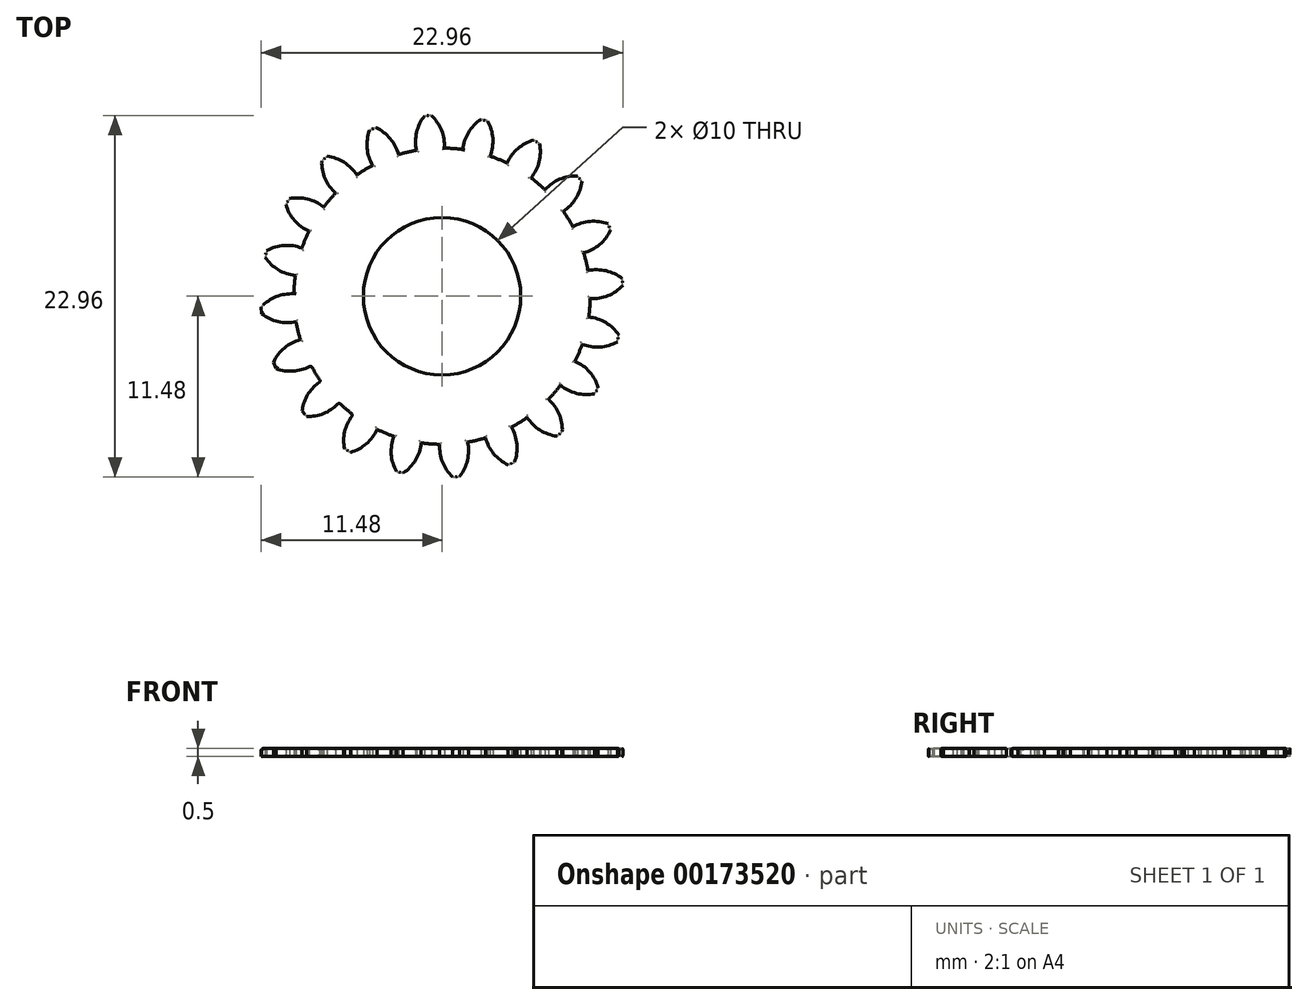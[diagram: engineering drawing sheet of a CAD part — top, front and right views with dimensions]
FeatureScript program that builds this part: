
annotation { "Feature Type Name" : "Feature", "Feature Type Description" : "" }
export const myFeature = defineFeature(function(context is Context, id is Id, definition is map)
    precondition{}
    {
        {
            assignVariable(context, id + "F0", {"name" : "GearDepth", "anyValue" : 0.5});
        }
        {
            assignVariable(context, id + "F1", {"name" : "TeethFillet", "anyValue" : getVariable(context, 'GearDepth') * .25});
        }
        {
            var Q0;
            Q0=qCreatedBy(makeId("Top.planeOp"),FACE);
            var sketch = newSketch(context, id + "F2", { "sketchPlane" : qUnion([Q0])});
            skCircle(sketch, "E0", {"center": v(0, 0) * mm, "radius": 9.4 * mm});
            skCircle(sketch, "E1", {"center": v(0, 0) * mm, "radius": 10.45 * mm, "construction": true});
            skCircle(sketch, "E2", {"center": v(0, 0) * mm, "radius": 11.5 * mm, "construction": true});
            skLineSegment(sketch, "E3", {"start": v(0, 0) * mm, "end": v(0, 17.6) * mm, "construction": true});
            skLineSegment(sketch, "E4", {"start": v(0, 0) * mm, "end": v(-1.42, 18) * mm, "construction": true});
            skLineSegment(sketch, "E5", {"start": v(0, 10.45) * mm, "end": v(-10.54, 10.45) * mm, "construction": true});
            skLineSegment(sketch, "E6", {"start": v(0, 10.45) * mm, "end": v(-10.3, 6.7) * mm, "construction": true});
            skCircle(sketch, "E7", {"center": v(0, 10.45) * mm, "radius": 2.61 * mm, "construction": true});
            skCircle(sketch, "E8", {"center": v(-2.46, 9.56) * mm, "radius": 2.61 * mm, "construction": true});
            skArc(sketch, "E9", {"start": v(-4.91, 10.45) * mm, "mid": v(-4.92, 10.42) * mm, "end": v(-4.94, 10.39) * mm});
            skArc(sketch, "E10.trimOffspring", {"start": v(0.15, 9.4) * mm, "mid": v(-0.03, 10.54) * mm, "end": v(-0.68, 11.48) * mm});
            skArc(sketch, "E11.MirrorCS", {"start": v(-1.62, 9.27) * mm, "mid": v(-1.62, 10.41) * mm, "end": v(-1.12, 11.45) * mm});
            skLineSegment(sketch, "E12", {"start": v(-1.12, 11.45) * mm, "end": v(-0.68, 11.48) * mm});
            skArc(sketch, "E13.1.0", {"start": v(-2.76, 9) * mm, "mid": v(-3.29, 10.01) * mm, "end": v(-4.2, 10.7) * mm});
            skLineSegment(sketch, "E13.1.1", {"start": v(-4.6, 10.54) * mm, "end": v(-4.2, 10.7) * mm});
            skArc(sketch, "E13.1.2", {"start": v(-4.4, 8.31) * mm, "mid": v(-4.76, 9.4) * mm, "end": v(-4.6, 10.54) * mm});
            skArc(sketch, "E13.2.0", {"start": v(-5.4, 7.7) * mm, "mid": v(-6.22, 8.5) * mm, "end": v(-7.3, 8.89) * mm});
            skLineSegment(sketch, "E13.2.1", {"start": v(-7.64, 8.6) * mm, "end": v(-7.3, 8.89) * mm});
            skArc(sketch, "E13.2.2", {"start": v(-6.76, 6.54) * mm, "mid": v(-7.43, 7.47) * mm, "end": v(-7.64, 8.6) * mm});
            skArc(sketch, "E13.3.0", {"start": v(-7.52, 5.65) * mm, "mid": v(-8.54, 6.17) * mm, "end": v(-9.69, 6.2) * mm});
            skLineSegment(sketch, "E13.3.1", {"start": v(-9.92, 5.82) * mm, "end": v(-9.69, 6.2) * mm});
            skArc(sketch, "E13.3.2", {"start": v(-8.45, 4.13) * mm, "mid": v(-9.37, 4.81) * mm, "end": v(-9.92, 5.82) * mm});
            skArc(sketch, "E13.4.0", {"start": v(-8.9, 3.05) * mm, "mid": v(-10.03, 3.23) * mm, "end": v(-11.13, 2.9) * mm});
            skLineSegment(sketch, "E13.4.1", {"start": v(-11.23, 2.47) * mm, "end": v(-11.13, 2.9) * mm});
            skArc(sketch, "E13.4.2", {"start": v(-9.32, 1.32) * mm, "mid": v(-10.4, 1.68) * mm, "end": v(-11.23, 2.47) * mm});
            skArc(sketch, "E13.5.0", {"start": v(-9.4, 0.15) * mm, "mid": v(-10.54, -0.03) * mm, "end": v(-11.48, -0.68) * mm});
            skLineSegment(sketch, "E13.5.1", {"start": v(-11.45, -1.12) * mm, "end": v(-11.48, -0.68) * mm});
            skArc(sketch, "E13.5.2", {"start": v(-9.27, -1.62) * mm, "mid": v(-10.41, -1.62) * mm, "end": v(-11.45, -1.12) * mm});
            skArc(sketch, "E13.6.0", {"start": v(-9, -2.76) * mm, "mid": v(-10.01, -3.29) * mm, "end": v(-10.7, -4.2) * mm});
            skLineSegment(sketch, "E13.6.1", {"start": v(-10.54, -4.6) * mm, "end": v(-10.7, -4.2) * mm});
            skArc(sketch, "E13.6.2", {"start": v(-8.31, -4.4) * mm, "mid": v(-9.4, -4.76) * mm, "end": v(-10.54, -4.6) * mm});
            skArc(sketch, "E13.7.0", {"start": v(-7.7, -5.4) * mm, "mid": v(-8.5, -6.22) * mm, "end": v(-8.89, -7.3) * mm});
            skLineSegment(sketch, "E13.7.1", {"start": v(-8.6, -7.64) * mm, "end": v(-8.89, -7.3) * mm});
            skArc(sketch, "E13.7.2", {"start": v(-6.54, -6.76) * mm, "mid": v(-7.47, -7.43) * mm, "end": v(-8.6, -7.64) * mm});
            skArc(sketch, "E13.8.0", {"start": v(-5.65, -7.52) * mm, "mid": v(-6.17, -8.54) * mm, "end": v(-6.2, -9.69) * mm});
            skLineSegment(sketch, "E13.8.1", {"start": v(-5.82, -9.92) * mm, "end": v(-6.2, -9.69) * mm});
            skArc(sketch, "E13.8.2", {"start": v(-4.13, -8.45) * mm, "mid": v(-4.81, -9.37) * mm, "end": v(-5.82, -9.92) * mm});
            skArc(sketch, "E13.9.0", {"start": v(-3.05, -8.9) * mm, "mid": v(-3.23, -10.03) * mm, "end": v(-2.9, -11.13) * mm});
            skLineSegment(sketch, "E13.9.1", {"start": v(-2.47, -11.23) * mm, "end": v(-2.9, -11.13) * mm});
            skArc(sketch, "E13.9.2", {"start": v(-1.32, -9.32) * mm, "mid": v(-1.68, -10.4) * mm, "end": v(-2.47, -11.23) * mm});
            skArc(sketch, "E13.10.0", {"start": v(-0.15, -9.4) * mm, "mid": v(0.03, -10.54) * mm, "end": v(0.68, -11.48) * mm});
            skLineSegment(sketch, "E13.10.1", {"start": v(1.12, -11.45) * mm, "end": v(0.68, -11.48) * mm});
            skArc(sketch, "E13.10.2", {"start": v(1.62, -9.27) * mm, "mid": v(1.62, -10.41) * mm, "end": v(1.12, -11.45) * mm});
            skArc(sketch, "E13.11.0", {"start": v(2.76, -9) * mm, "mid": v(3.29, -10.01) * mm, "end": v(4.2, -10.7) * mm});
            skLineSegment(sketch, "E13.11.1", {"start": v(4.6, -10.54) * mm, "end": v(4.2, -10.7) * mm});
            skArc(sketch, "E13.11.2", {"start": v(4.4, -8.31) * mm, "mid": v(4.76, -9.4) * mm, "end": v(4.6, -10.54) * mm});
            skArc(sketch, "E13.12.0", {"start": v(5.4, -7.7) * mm, "mid": v(6.22, -8.5) * mm, "end": v(7.3, -8.89) * mm});
            skLineSegment(sketch, "E13.12.1", {"start": v(7.64, -8.6) * mm, "end": v(7.3, -8.89) * mm});
            skArc(sketch, "E13.12.2", {"start": v(6.76, -6.54) * mm, "mid": v(7.43, -7.47) * mm, "end": v(7.64, -8.6) * mm});
            skArc(sketch, "E13.13.0", {"start": v(7.52, -5.65) * mm, "mid": v(8.54, -6.17) * mm, "end": v(9.69, -6.2) * mm});
            skLineSegment(sketch, "E13.13.1", {"start": v(9.92, -5.82) * mm, "end": v(9.69, -6.2) * mm});
            skArc(sketch, "E13.13.2", {"start": v(8.45, -4.13) * mm, "mid": v(9.37, -4.81) * mm, "end": v(9.92, -5.82) * mm});
            skArc(sketch, "E13.14.0", {"start": v(8.9, -3.05) * mm, "mid": v(10.03, -3.23) * mm, "end": v(11.13, -2.9) * mm});
            skLineSegment(sketch, "E13.14.1", {"start": v(11.23, -2.47) * mm, "end": v(11.13, -2.9) * mm});
            skArc(sketch, "E13.14.2", {"start": v(9.32, -1.32) * mm, "mid": v(10.4, -1.68) * mm, "end": v(11.23, -2.47) * mm});
            skArc(sketch, "E13.15.0", {"start": v(9.4, -0.15) * mm, "mid": v(10.54, 0.03) * mm, "end": v(11.48, 0.68) * mm});
            skLineSegment(sketch, "E13.15.1", {"start": v(11.45, 1.12) * mm, "end": v(11.48, 0.68) * mm});
            skArc(sketch, "E13.15.2", {"start": v(9.27, 1.62) * mm, "mid": v(10.41, 1.62) * mm, "end": v(11.45, 1.12) * mm});
            skArc(sketch, "E13.16.0", {"start": v(9, 2.76) * mm, "mid": v(10.01, 3.29) * mm, "end": v(10.7, 4.2) * mm});
            skLineSegment(sketch, "E13.16.1", {"start": v(10.54, 4.6) * mm, "end": v(10.7, 4.2) * mm});
            skArc(sketch, "E13.16.2", {"start": v(8.31, 4.4) * mm, "mid": v(9.4, 4.76) * mm, "end": v(10.54, 4.6) * mm});
            skArc(sketch, "E13.17.0", {"start": v(7.7, 5.4) * mm, "mid": v(8.5, 6.22) * mm, "end": v(8.89, 7.3) * mm});
            skLineSegment(sketch, "E13.17.1", {"start": v(8.6, 7.64) * mm, "end": v(8.89, 7.3) * mm});
            skArc(sketch, "E13.17.2", {"start": v(6.54, 6.76) * mm, "mid": v(7.47, 7.43) * mm, "end": v(8.6, 7.64) * mm});
            skArc(sketch, "E13.18.0", {"start": v(5.65, 7.52) * mm, "mid": v(6.17, 8.54) * mm, "end": v(6.2, 9.69) * mm});
            skLineSegment(sketch, "E13.18.1", {"start": v(5.82, 9.92) * mm, "end": v(6.2, 9.69) * mm});
            skArc(sketch, "E13.18.2", {"start": v(4.13, 8.45) * mm, "mid": v(4.81, 9.37) * mm, "end": v(5.82, 9.92) * mm});
            skArc(sketch, "E13.19.0", {"start": v(3.05, 8.9) * mm, "mid": v(3.23, 10.03) * mm, "end": v(2.9, 11.13) * mm});
            skLineSegment(sketch, "E13.19.1", {"start": v(2.47, 11.23) * mm, "end": v(2.9, 11.13) * mm});
            skArc(sketch, "E13.19.2", {"start": v(1.32, 9.32) * mm, "mid": v(1.68, 10.4) * mm, "end": v(2.47, 11.23) * mm});
            skCircle(sketch, "E14", {"center": v(0, 0) * mm, "radius": 5 * mm});
            skSolve(sketch);
        }
        {
            var Q0;
            {var subQ0=sQuery(id+"F2.wireOp",EDGE,"E10.trimOffspring");Q0=makeQuery(id+"F2.imprint","IMPRINT",FACE,{"disambiguationData":[TD([[makeQuery(id+"F2.imprint","IMPRINT",EDGE,{"derivedFrom":subQ0}),1.0]])]});}
            var Q1;
            {var subQ0=sQuery(id+"F2.wireOp",EDGE,"E0");var subQ1=makeQuery(id+"F2.imprint","INTERSECT",VERTEX,{"derivedFrom":[subQ0,sQuery(id+"F2.wireOp",EDGE,"E10.trimOffspring")]});Q1=makeQuery(id+"F2.imprint","IMPRINT",FACE,{"disambiguationData":[TD([[makeQuery(id+"F2.imprint","IMPRINT",EDGE,{"disambiguationData":[TD([[subQ1,-1.0]])],"derivedFrom":subQ0}),1.0]])]});}
            var Q2;
            {var subQ0=sQuery(id+"F2.wireOp",EDGE,"E13.1.0");Q2=makeQuery(id+"F2.imprint","IMPRINT",FACE,{"disambiguationData":[TD([[makeQuery(id+"F2.imprint","IMPRINT",EDGE,{"derivedFrom":subQ0}),1.0]])]});}
            var Q3;
            {var subQ0=sQuery(id+"F2.wireOp",EDGE,"E13.2.0");Q3=makeQuery(id+"F2.imprint","IMPRINT",FACE,{"disambiguationData":[TD([[makeQuery(id+"F2.imprint","IMPRINT",EDGE,{"derivedFrom":subQ0}),1.0]])]});}
            var Q4;
            {var subQ0=sQuery(id+"F2.wireOp",EDGE,"E13.3.0");Q4=makeQuery(id+"F2.imprint","IMPRINT",FACE,{"disambiguationData":[TD([[makeQuery(id+"F2.imprint","IMPRINT",EDGE,{"derivedFrom":subQ0}),1.0]])]});}
            var Q5;
            {var subQ0=sQuery(id+"F2.wireOp",EDGE,"E13.4.0");Q5=makeQuery(id+"F2.imprint","IMPRINT",FACE,{"disambiguationData":[TD([[makeQuery(id+"F2.imprint","IMPRINT",EDGE,{"derivedFrom":subQ0}),1.0]])]});}
            var Q6;
            {var subQ0=sQuery(id+"F2.wireOp",EDGE,"E13.5.0");Q6=makeQuery(id+"F2.imprint","IMPRINT",FACE,{"disambiguationData":[TD([[makeQuery(id+"F2.imprint","IMPRINT",EDGE,{"derivedFrom":subQ0}),1.0]])]});}
            var Q7;
            {var subQ0=sQuery(id+"F2.wireOp",EDGE,"E13.6.0");Q7=makeQuery(id+"F2.imprint","IMPRINT",FACE,{"disambiguationData":[TD([[makeQuery(id+"F2.imprint","IMPRINT",EDGE,{"derivedFrom":subQ0}),1.0]])]});}
            var Q8;
            {var subQ0=sQuery(id+"F2.wireOp",EDGE,"E13.7.0");Q8=makeQuery(id+"F2.imprint","IMPRINT",FACE,{"disambiguationData":[TD([[makeQuery(id+"F2.imprint","IMPRINT",EDGE,{"derivedFrom":subQ0}),1.0]])]});}
            var Q9;
            {var subQ0=sQuery(id+"F2.wireOp",EDGE,"E13.8.0");Q9=makeQuery(id+"F2.imprint","IMPRINT",FACE,{"disambiguationData":[TD([[makeQuery(id+"F2.imprint","IMPRINT",EDGE,{"derivedFrom":subQ0}),1.0]])]});}
            var Q10;
            {var subQ0=sQuery(id+"F2.wireOp",EDGE,"E13.9.0");Q10=makeQuery(id+"F2.imprint","IMPRINT",FACE,{"disambiguationData":[TD([[makeQuery(id+"F2.imprint","IMPRINT",EDGE,{"derivedFrom":subQ0}),1.0]])]});}
            var Q11;
            {var subQ0=sQuery(id+"F2.wireOp",EDGE,"E13.10.0");Q11=makeQuery(id+"F2.imprint","IMPRINT",FACE,{"disambiguationData":[TD([[makeQuery(id+"F2.imprint","IMPRINT",EDGE,{"derivedFrom":subQ0}),1.0]])]});}
            var Q12;
            {var subQ0=sQuery(id+"F2.wireOp",EDGE,"E13.11.0");Q12=makeQuery(id+"F2.imprint","IMPRINT",FACE,{"disambiguationData":[TD([[makeQuery(id+"F2.imprint","IMPRINT",EDGE,{"derivedFrom":subQ0}),1.0]])]});}
            var Q13;
            {var subQ0=sQuery(id+"F2.wireOp",EDGE,"E13.12.0");Q13=makeQuery(id+"F2.imprint","IMPRINT",FACE,{"disambiguationData":[TD([[makeQuery(id+"F2.imprint","IMPRINT",EDGE,{"derivedFrom":subQ0}),1.0]])]});}
            var Q14;
            {var subQ0=sQuery(id+"F2.wireOp",EDGE,"E13.13.0");Q14=makeQuery(id+"F2.imprint","IMPRINT",FACE,{"disambiguationData":[TD([[makeQuery(id+"F2.imprint","IMPRINT",EDGE,{"derivedFrom":subQ0}),1.0]])]});}
            var Q15;
            {var subQ0=sQuery(id+"F2.wireOp",EDGE,"E13.14.0");Q15=makeQuery(id+"F2.imprint","IMPRINT",FACE,{"disambiguationData":[TD([[makeQuery(id+"F2.imprint","IMPRINT",EDGE,{"derivedFrom":subQ0}),1.0]])]});}
            var Q16;
            {var subQ0=sQuery(id+"F2.wireOp",EDGE,"E13.15.0");Q16=makeQuery(id+"F2.imprint","IMPRINT",FACE,{"disambiguationData":[TD([[makeQuery(id+"F2.imprint","IMPRINT",EDGE,{"derivedFrom":subQ0}),1.0]])]});}
            var Q17;
            {var subQ0=sQuery(id+"F2.wireOp",EDGE,"E13.16.0");Q17=makeQuery(id+"F2.imprint","IMPRINT",FACE,{"disambiguationData":[TD([[makeQuery(id+"F2.imprint","IMPRINT",EDGE,{"derivedFrom":subQ0}),1.0]])]});}
            var Q18;
            {var subQ0=sQuery(id+"F2.wireOp",EDGE,"E13.17.0");Q18=makeQuery(id+"F2.imprint","IMPRINT",FACE,{"disambiguationData":[TD([[makeQuery(id+"F2.imprint","IMPRINT",EDGE,{"derivedFrom":subQ0}),1.0]])]});}
            var Q19;
            {var subQ0=sQuery(id+"F2.wireOp",EDGE,"E13.18.0");Q19=makeQuery(id+"F2.imprint","IMPRINT",FACE,{"disambiguationData":[TD([[makeQuery(id+"F2.imprint","IMPRINT",EDGE,{"derivedFrom":subQ0}),1.0]])]});}
            var Q20;
            {var subQ0=sQuery(id+"F2.wireOp",EDGE,"E13.19.0");Q20=makeQuery(id+"F2.imprint","IMPRINT",FACE,{"disambiguationData":[TD([[makeQuery(id+"F2.imprint","IMPRINT",EDGE,{"derivedFrom":subQ0}),1.0]])]});}
            var Q21;
            Q21=sQuery(id+"F2.wireOp",EDGE,"E0");
            var Q22;
            Q22=sQuery(id+"F2.wireOp",EDGE,"E10.trimOffspring");
            var Q23;
            Q23=sQuery(id+"F2.wireOp",EDGE,"E12");
            var Q24;
            Q24=sQuery(id+"F2.wireOp",EDGE,"E11.MirrorCS");
            extrude(context, id + "F3", {"entities" : qUnion([Q0, Q1, Q2, Q3, Q4, Q5, Q6, Q7, Q8, Q9, Q10, Q11, Q12, Q13, Q14, Q15, Q16, Q17, Q18, Q19, Q20]), "surfaceEntities" : qUnion([Q21, Q22, Q23, Q24]), "depth" : (getVariable(context, 'GearDepth')) * mm});
        }
        {
            var Q0;
            Q0=makeQuery(id+"F3.opExtrude","CAP_EDGE",EDGE,{"disambiguationData":[OSD([sQuery(id+"F2.wireOp",EDGE,"E13.5.2")])],"isStart":false});
            var Q1;
            Q1=makeQuery(id+"F3.opExtrude","CAP_EDGE",EDGE,{"disambiguationData":[OSD([sQuery(id+"F2.wireOp",EDGE,"E13.5.1")])],"isStart":false});
            var Q2;
            {var subQ0=sQuery(id+"F2.wireOp",EDGE,"E0");Q2=makeQuery(id+"F3.opExtrude","CAP_EDGE",EDGE,{"disambiguationData":[OSD([subQ0]),TDD([makeQuery(id+"F2.imprint","IMPRINT",EDGE,{"disambiguationData":[TD([[makeQuery(id+"F2.imprint","INTERSECT",VERTEX,{"derivedFrom":[subQ0,sQuery(id+"F2.wireOp",EDGE,"E13.5.2")]}),-1.0]])],"derivedFrom":subQ0})])],"isStart":false});}
            var Q3;
            Q3=makeQuery(id+"F3.opExtrude","CAP_EDGE",EDGE,{"disambiguationData":[OSD([sQuery(id+"F2.wireOp",EDGE,"E13.6.0")])],"isStart":false});
            var Q4;
            Q4=makeQuery(id+"F3.opExtrude","CAP_EDGE",EDGE,{"disambiguationData":[OSD([sQuery(id+"F2.wireOp",EDGE,"E13.6.1")])],"isStart":false});
            var Q5;
            Q5=makeQuery(id+"F3.opExtrude","CAP_EDGE",EDGE,{"disambiguationData":[OSD([sQuery(id+"F2.wireOp",EDGE,"E13.6.2")])],"isStart":false});
            var Q6;
            {var subQ0=sQuery(id+"F2.wireOp",EDGE,"E0");Q6=makeQuery(id+"F3.opExtrude","SWEPT_FACE",FACE,{"disambiguationData":[OSD([subQ0]),TDD([makeQuery(id+"F2.imprint","IMPRINT",EDGE,{"disambiguationData":[TD([[makeQuery(id+"F2.imprint","INTERSECT",VERTEX,{"derivedFrom":[subQ0,sQuery(id+"F2.wireOp",EDGE,"E13.6.2")]}),-1.0]])],"derivedFrom":subQ0})])]});}
            var Q7;
            {var subQ0=sQuery(id+"F2.wireOp",EDGE,"E0");Q7=makeQuery(id+"F3.opExtrude","CAP_EDGE",EDGE,{"disambiguationData":[OSD([subQ0]),TDD([makeQuery(id+"F2.imprint","IMPRINT",EDGE,{"disambiguationData":[TD([[makeQuery(id+"F2.imprint","INTERSECT",VERTEX,{"derivedFrom":[subQ0,sQuery(id+"F2.wireOp",EDGE,"E13.6.2")]}),-1.0]])],"derivedFrom":subQ0})])],"isStart":false});}
            var Q8;
            Q8=makeQuery(id+"F3.opExtrude","CAP_EDGE",EDGE,{"disambiguationData":[OSD([sQuery(id+"F2.wireOp",EDGE,"E13.7.2")])],"isStart":true});
            var Q9;
            {var subQ0=sQuery(id+"F2.wireOp",EDGE,"E0");Q9=makeQuery(id+"F3.opExtrude","CAP_EDGE",EDGE,{"disambiguationData":[OSD([subQ0]),TDD([makeQuery(id+"F2.imprint","IMPRINT",EDGE,{"disambiguationData":[TD([[makeQuery(id+"F2.imprint","INTERSECT",VERTEX,{"derivedFrom":[subQ0,sQuery(id+"F2.wireOp",EDGE,"E13.7.2")]}),-1.0]])],"derivedFrom":subQ0})])],"isStart":true});}
            var Q10;
            Q10=makeQuery(id+"F3.opExtrude","CAP_EDGE",EDGE,{"disambiguationData":[OSD([sQuery(id+"F2.wireOp",EDGE,"E13.7.2")])],"isStart":false});
            var Q11;
            {var subQ0=sQuery(id+"F2.wireOp",EDGE,"E0");Q11=makeQuery(id+"F3.opExtrude","CAP_EDGE",EDGE,{"disambiguationData":[OSD([subQ0]),TDD([makeQuery(id+"F2.imprint","IMPRINT",EDGE,{"disambiguationData":[TD([[makeQuery(id+"F2.imprint","INTERSECT",VERTEX,{"derivedFrom":[subQ0,sQuery(id+"F2.wireOp",EDGE,"E13.7.2")]}),-1.0]])],"derivedFrom":subQ0})])],"isStart":false});}
            var Q12;
            Q12=makeQuery(id+"F3.opExtrude","CAP_EDGE",EDGE,{"disambiguationData":[OSD([sQuery(id+"F2.wireOp",EDGE,"E13.8.0")])],"isStart":false});
            var Q13;
            {var subQ0=sQuery(id+"F2.wireOp",EDGE,"E0");Q13=makeQuery(id+"F3.opExtrude","SWEPT_FACE",FACE,{"disambiguationData":[OSD([subQ0]),TDD([makeQuery(id+"F2.imprint","IMPRINT",EDGE,{"disambiguationData":[TD([[makeQuery(id+"F2.imprint","INTERSECT",VERTEX,{"derivedFrom":[subQ0,sQuery(id+"F2.wireOp",EDGE,"E13.7.2")]}),-1.0]])],"derivedFrom":subQ0})])]});}
            var Q14;
            Q14=makeQuery(id+"F3.opExtrude","CAP_EDGE",EDGE,{"disambiguationData":[OSD([sQuery(id+"F2.wireOp",EDGE,"E13.6.0")])],"isStart":true});
            var Q15;
            Q15=makeQuery(id+"F3.opExtrude","CAP_EDGE",EDGE,{"disambiguationData":[OSD([sQuery(id+"F2.wireOp",EDGE,"E13.8.2")])],"isStart":false});
            var Q16;
            {var subQ0=sQuery(id+"F2.wireOp",EDGE,"E0");Q16=makeQuery(id+"F3.opExtrude","CAP_EDGE",EDGE,{"disambiguationData":[OSD([subQ0]),TDD([makeQuery(id+"F2.imprint","IMPRINT",EDGE,{"disambiguationData":[TD([[makeQuery(id+"F2.imprint","INTERSECT",VERTEX,{"derivedFrom":[subQ0,sQuery(id+"F2.wireOp",EDGE,"E13.8.2")]}),-1.0]])],"derivedFrom":subQ0})])],"isStart":false});}
            var Q17;
            Q17=makeQuery(id+"F3.opExtrude","CAP_EDGE",EDGE,{"disambiguationData":[OSD([sQuery(id+"F2.wireOp",EDGE,"E13.9.0")])],"isStart":false});
            var Q18;
            Q18=makeQuery(id+"F3.opExtrude","CAP_EDGE",EDGE,{"disambiguationData":[OSD([sQuery(id+"F2.wireOp",EDGE,"E13.9.2")])],"isStart":false});
            var Q19;
            {var subQ0=sQuery(id+"F2.wireOp",EDGE,"E0");Q19=makeQuery(id+"F3.opExtrude","CAP_EDGE",EDGE,{"disambiguationData":[OSD([subQ0]),TDD([makeQuery(id+"F2.imprint","IMPRINT",EDGE,{"disambiguationData":[TD([[makeQuery(id+"F2.imprint","INTERSECT",VERTEX,{"derivedFrom":[subQ0,sQuery(id+"F2.wireOp",EDGE,"E13.9.2")]}),-1.0]])],"derivedFrom":subQ0})])],"isStart":false});}
            var Q20;
            Q20=makeQuery(id+"F3.opExtrude","CAP_EDGE",EDGE,{"disambiguationData":[OSD([sQuery(id+"F2.wireOp",EDGE,"E13.10.0")])],"isStart":false});
            var Q21;
            Q21=makeQuery(id+"F3.opExtrude","CAP_EDGE",EDGE,{"disambiguationData":[OSD([sQuery(id+"F2.wireOp",EDGE,"E13.10.2")])],"isStart":false});
            var Q22;
            {var subQ0=sQuery(id+"F2.wireOp",EDGE,"E0");Q22=makeQuery(id+"F3.opExtrude","CAP_EDGE",EDGE,{"disambiguationData":[OSD([subQ0]),TDD([makeQuery(id+"F2.imprint","IMPRINT",EDGE,{"disambiguationData":[TD([[makeQuery(id+"F2.imprint","INTERSECT",VERTEX,{"derivedFrom":[subQ0,sQuery(id+"F2.wireOp",EDGE,"E13.10.2")]}),-1.0]])],"derivedFrom":subQ0})])],"isStart":false});}
            var Q23;
            Q23=makeQuery(id+"F3.opExtrude","CAP_EDGE",EDGE,{"disambiguationData":[OSD([sQuery(id+"F2.wireOp",EDGE,"E13.11.0")])],"isStart":false});
            var Q24;
            Q24=makeQuery(id+"F3.opExtrude","CAP_EDGE",EDGE,{"disambiguationData":[OSD([sQuery(id+"F2.wireOp",EDGE,"E13.11.2")])],"isStart":false});
            var Q25;
            {var subQ0=sQuery(id+"F2.wireOp",EDGE,"E0");Q25=makeQuery(id+"F3.opExtrude","CAP_EDGE",EDGE,{"disambiguationData":[OSD([subQ0]),TDD([makeQuery(id+"F2.imprint","IMPRINT",EDGE,{"disambiguationData":[TD([[makeQuery(id+"F2.imprint","INTERSECT",VERTEX,{"derivedFrom":[subQ0,sQuery(id+"F2.wireOp",EDGE,"E13.11.2")]}),-1.0]])],"derivedFrom":subQ0})])],"isStart":false});}
            var Q26;
            Q26=makeQuery(id+"F3.opExtrude","CAP_EDGE",EDGE,{"disambiguationData":[OSD([sQuery(id+"F2.wireOp",EDGE,"E13.12.0")])],"isStart":false});
            var Q27;
            Q27=makeQuery(id+"F3.opExtrude","CAP_EDGE",EDGE,{"disambiguationData":[OSD([sQuery(id+"F2.wireOp",EDGE,"E13.12.2")])],"isStart":false});
            var Q28;
            {var subQ0=sQuery(id+"F2.wireOp",EDGE,"E0");Q28=makeQuery(id+"F3.opExtrude","CAP_EDGE",EDGE,{"disambiguationData":[OSD([subQ0]),TDD([makeQuery(id+"F2.imprint","IMPRINT",EDGE,{"disambiguationData":[TD([[makeQuery(id+"F2.imprint","INTERSECT",VERTEX,{"derivedFrom":[subQ0,sQuery(id+"F2.wireOp",EDGE,"E13.12.2")]}),-1.0]])],"derivedFrom":subQ0})])],"isStart":false});}
            var Q29;
            Q29=makeQuery(id+"F3.opExtrude","CAP_EDGE",EDGE,{"disambiguationData":[OSD([sQuery(id+"F2.wireOp",EDGE,"E13.13.0")])],"isStart":false});
            var Q30;
            Q30=makeQuery(id+"F3.opExtrude","CAP_EDGE",EDGE,{"disambiguationData":[OSD([sQuery(id+"F2.wireOp",EDGE,"E13.13.2")])],"isStart":false});
            var Q31;
            {var subQ0=sQuery(id+"F2.wireOp",EDGE,"E0");Q31=makeQuery(id+"F3.opExtrude","CAP_EDGE",EDGE,{"disambiguationData":[OSD([subQ0]),TDD([makeQuery(id+"F2.imprint","IMPRINT",EDGE,{"disambiguationData":[TD([[makeQuery(id+"F2.imprint","INTERSECT",VERTEX,{"derivedFrom":[subQ0,sQuery(id+"F2.wireOp",EDGE,"E13.13.2")]}),-1.0]])],"derivedFrom":subQ0})])],"isStart":false});}
            var Q32;
            Q32=makeQuery(id+"F3.opExtrude","CAP_EDGE",EDGE,{"disambiguationData":[OSD([sQuery(id+"F2.wireOp",EDGE,"E13.14.0")])],"isStart":false});
            var Q33;
            Q33=makeQuery(id+"F3.opExtrude","CAP_EDGE",EDGE,{"disambiguationData":[OSD([sQuery(id+"F2.wireOp",EDGE,"E13.14.2")])],"isStart":false});
            var Q34;
            {var subQ0=sQuery(id+"F2.wireOp",EDGE,"E0");Q34=makeQuery(id+"F3.opExtrude","CAP_EDGE",EDGE,{"disambiguationData":[OSD([subQ0]),TDD([makeQuery(id+"F2.imprint","IMPRINT",EDGE,{"disambiguationData":[TD([[makeQuery(id+"F2.imprint","INTERSECT",VERTEX,{"derivedFrom":[subQ0,sQuery(id+"F2.wireOp",EDGE,"E13.14.2")]}),-1.0]])],"derivedFrom":subQ0})])],"isStart":false});}
            var Q35;
            Q35=makeQuery(id+"F3.opExtrude","CAP_EDGE",EDGE,{"disambiguationData":[OSD([sQuery(id+"F2.wireOp",EDGE,"E13.15.0")])],"isStart":false});
            var Q36;
            {var subQ0=sQuery(id+"F2.wireOp",EDGE,"E0");Q36=makeQuery(id+"F3.opExtrude","CAP_EDGE",EDGE,{"disambiguationData":[OSD([subQ0]),TDD([makeQuery(id+"F2.imprint","IMPRINT",EDGE,{"disambiguationData":[TD([[makeQuery(id+"F2.imprint","INTERSECT",VERTEX,{"derivedFrom":[subQ0,sQuery(id+"F2.wireOp",EDGE,"E13.14.2")]}),-1.0]])],"derivedFrom":subQ0})])],"isStart":false});}
            var Q37;
            Q37=makeQuery(id+"F3.opExtrude","CAP_EDGE",EDGE,{"disambiguationData":[OSD([sQuery(id+"F2.wireOp",EDGE,"E13.15.2")])],"isStart":false});
            var Q38;
            {var subQ0=sQuery(id+"F2.wireOp",EDGE,"E0");Q38=makeQuery(id+"F3.opExtrude","CAP_EDGE",EDGE,{"disambiguationData":[OSD([subQ0]),TDD([makeQuery(id+"F2.imprint","IMPRINT",EDGE,{"disambiguationData":[TD([[makeQuery(id+"F2.imprint","INTERSECT",VERTEX,{"derivedFrom":[subQ0,sQuery(id+"F2.wireOp",EDGE,"E13.15.2")]}),-1.0]])],"derivedFrom":subQ0})])],"isStart":false});}
            var Q39;
            Q39=makeQuery(id+"F3.opExtrude","CAP_EDGE",EDGE,{"disambiguationData":[OSD([sQuery(id+"F2.wireOp",EDGE,"E13.16.0")])],"isStart":false});
            var Q40;
            Q40=makeQuery(id+"F3.opExtrude","CAP_EDGE",EDGE,{"disambiguationData":[OSD([sQuery(id+"F2.wireOp",EDGE,"E13.16.2")])],"isStart":false});
            var Q41;
            Q41=makeQuery(id+"F3.opExtrude","CAP_EDGE",EDGE,{"disambiguationData":[OSD([sQuery(id+"F2.wireOp",EDGE,"E13.17.0")])],"isStart":false});
            var Q42;
            {var subQ0=sQuery(id+"F2.wireOp",EDGE,"E0");Q42=makeQuery(id+"F3.opExtrude","CAP_EDGE",EDGE,{"disambiguationData":[OSD([subQ0]),TDD([makeQuery(id+"F2.imprint","IMPRINT",EDGE,{"disambiguationData":[TD([[makeQuery(id+"F2.imprint","INTERSECT",VERTEX,{"derivedFrom":[subQ0,sQuery(id+"F2.wireOp",EDGE,"E13.16.2")]}),-1.0]])],"derivedFrom":subQ0})])],"isStart":false});}
            var Q43;
            Q43=makeQuery(id+"F3.opExtrude","CAP_EDGE",EDGE,{"disambiguationData":[OSD([sQuery(id+"F2.wireOp",EDGE,"E13.17.2")])],"isStart":false});
            var Q44;
            {var subQ0=sQuery(id+"F2.wireOp",EDGE,"E0");Q44=makeQuery(id+"F3.opExtrude","CAP_EDGE",EDGE,{"disambiguationData":[OSD([subQ0]),TDD([makeQuery(id+"F2.imprint","IMPRINT",EDGE,{"disambiguationData":[TD([[makeQuery(id+"F2.imprint","INTERSECT",VERTEX,{"derivedFrom":[subQ0,sQuery(id+"F2.wireOp",EDGE,"E13.17.2")]}),-1.0]])],"derivedFrom":subQ0})])],"isStart":false});}
            var Q45;
            Q45=makeQuery(id+"F3.opExtrude","CAP_EDGE",EDGE,{"disambiguationData":[OSD([sQuery(id+"F2.wireOp",EDGE,"E13.18.0")])],"isStart":false});
            var Q46;
            Q46=makeQuery(id+"F3.opExtrude","CAP_EDGE",EDGE,{"disambiguationData":[OSD([sQuery(id+"F2.wireOp",EDGE,"E13.18.2")])],"isStart":false});
            var Q47;
            {var subQ0=sQuery(id+"F2.wireOp",EDGE,"E0");Q47=makeQuery(id+"F3.opExtrude","CAP_EDGE",EDGE,{"disambiguationData":[OSD([subQ0]),TDD([makeQuery(id+"F2.imprint","IMPRINT",EDGE,{"disambiguationData":[TD([[makeQuery(id+"F2.imprint","INTERSECT",VERTEX,{"derivedFrom":[subQ0,sQuery(id+"F2.wireOp",EDGE,"E13.18.2")]}),-1.0]])],"derivedFrom":subQ0})])],"isStart":false});}
            var Q48;
            Q48=makeQuery(id+"F3.opExtrude","CAP_EDGE",EDGE,{"disambiguationData":[OSD([sQuery(id+"F2.wireOp",EDGE,"E13.19.0")])],"isStart":false});
            var Q49;
            Q49=makeQuery(id+"F3.opExtrude","CAP_EDGE",EDGE,{"disambiguationData":[OSD([sQuery(id+"F2.wireOp",EDGE,"E13.19.2")])],"isStart":false});
            var Q50;
            Q50=makeQuery(id+"F3.opExtrude","CAP_EDGE",EDGE,{"disambiguationData":[OSD([sQuery(id+"F2.wireOp",EDGE,"E10.trimOffspring")])],"isStart":false});
            var Q51;
            Q51=makeQuery(id+"F3.opExtrude","CAP_EDGE",EDGE,{"disambiguationData":[OSD([sQuery(id+"F2.wireOp",EDGE,"E11.MirrorCS")])],"isStart":false});
            var Q52;
            {var subQ0=sQuery(id+"F2.wireOp",EDGE,"E0");Q52=makeQuery(id+"F3.opExtrude","CAP_EDGE",EDGE,{"disambiguationData":[OSD([subQ0]),TDD([makeQuery(id+"F2.imprint","IMPRINT",EDGE,{"disambiguationData":[TD([[makeQuery(id+"F2.imprint","INTERSECT",VERTEX,{"derivedFrom":[subQ0,sQuery(id+"F2.wireOp",EDGE,"E11.MirrorCS")]}),-1.0]])],"derivedFrom":subQ0})])],"isStart":false});}
            var Q53;
            Q53=makeQuery(id+"F3.opExtrude","CAP_EDGE",EDGE,{"disambiguationData":[OSD([sQuery(id+"F2.wireOp",EDGE,"E13.1.0")])],"isStart":false});
            var Q54;
            Q54=makeQuery(id+"F3.opExtrude","CAP_EDGE",EDGE,{"disambiguationData":[OSD([sQuery(id+"F2.wireOp",EDGE,"E13.1.2")])],"isStart":false});
            var Q55;
            {var subQ0=sQuery(id+"F2.wireOp",EDGE,"E0");Q55=makeQuery(id+"F3.opExtrude","CAP_EDGE",EDGE,{"disambiguationData":[OSD([subQ0]),TDD([makeQuery(id+"F2.imprint","IMPRINT",EDGE,{"disambiguationData":[TD([[makeQuery(id+"F2.imprint","INTERSECT",VERTEX,{"derivedFrom":[subQ0,sQuery(id+"F2.wireOp",EDGE,"E13.1.2")]}),-1.0]])],"derivedFrom":subQ0})])],"isStart":false});}
            var Q56;
            Q56=makeQuery(id+"F3.opExtrude","CAP_EDGE",EDGE,{"disambiguationData":[OSD([sQuery(id+"F2.wireOp",EDGE,"E13.2.0")])],"isStart":false});
            var Q57;
            Q57=makeQuery(id+"F3.opExtrude","CAP_EDGE",EDGE,{"disambiguationData":[OSD([sQuery(id+"F2.wireOp",EDGE,"E13.2.2")])],"isStart":false});
            var Q58;
            {var subQ0=sQuery(id+"F2.wireOp",EDGE,"E0");Q58=makeQuery(id+"F3.opExtrude","CAP_EDGE",EDGE,{"disambiguationData":[OSD([subQ0]),TDD([makeQuery(id+"F2.imprint","IMPRINT",EDGE,{"disambiguationData":[TD([[makeQuery(id+"F2.imprint","INTERSECT",VERTEX,{"derivedFrom":[subQ0,sQuery(id+"F2.wireOp",EDGE,"E13.2.2")]}),-1.0]])],"derivedFrom":subQ0})])],"isStart":false});}
            var Q59;
            Q59=makeQuery(id+"F3.opExtrude","CAP_EDGE",EDGE,{"disambiguationData":[OSD([sQuery(id+"F2.wireOp",EDGE,"E13.3.0")])],"isStart":false});
            var Q60;
            Q60=makeQuery(id+"F3.opExtrude","CAP_EDGE",EDGE,{"disambiguationData":[OSD([sQuery(id+"F2.wireOp",EDGE,"E13.3.2")])],"isStart":false});
            var Q61;
            {var subQ0=sQuery(id+"F2.wireOp",EDGE,"E0");Q61=makeQuery(id+"F3.opExtrude","CAP_EDGE",EDGE,{"disambiguationData":[OSD([subQ0]),TDD([makeQuery(id+"F2.imprint","IMPRINT",EDGE,{"disambiguationData":[TD([[makeQuery(id+"F2.imprint","INTERSECT",VERTEX,{"derivedFrom":[subQ0,sQuery(id+"F2.wireOp",EDGE,"E13.3.2")]}),-1.0]])],"derivedFrom":subQ0})])],"isStart":false});}
            var Q62;
            Q62=makeQuery(id+"F3.opExtrude","CAP_EDGE",EDGE,{"disambiguationData":[OSD([sQuery(id+"F2.wireOp",EDGE,"E13.4.0")])],"isStart":false});
            var Q63;
            Q63=makeQuery(id+"F3.opExtrude","CAP_EDGE",EDGE,{"disambiguationData":[OSD([sQuery(id+"F2.wireOp",EDGE,"E13.4.2")])],"isStart":false});
            var Q64;
            {var subQ0=sQuery(id+"F2.wireOp",EDGE,"E0");Q64=makeQuery(id+"F3.opExtrude","CAP_EDGE",EDGE,{"disambiguationData":[OSD([subQ0]),TDD([makeQuery(id+"F2.imprint","IMPRINT",EDGE,{"disambiguationData":[TD([[makeQuery(id+"F2.imprint","INTERSECT",VERTEX,{"derivedFrom":[subQ0,sQuery(id+"F2.wireOp",EDGE,"E13.4.2")]}),-1.0]])],"derivedFrom":subQ0})])],"isStart":false});}
            var Q65;
            {var subQ0=sQuery(id+"F2.wireOp",EDGE,"E0");Q65=makeQuery(id+"F3.opExtrude","CAP_EDGE",EDGE,{"disambiguationData":[OSD([subQ0]),TDD([makeQuery(id+"F2.imprint","IMPRINT",EDGE,{"disambiguationData":[TD([[makeQuery(id+"F2.imprint","INTERSECT",VERTEX,{"derivedFrom":[subQ0,sQuery(id+"F2.wireOp",EDGE,"E13.5.2")]}),-1.0]])],"derivedFrom":subQ0})])],"isStart":true});}
            var Q66;
            Q66=makeQuery(id+"F3.opExtrude","CAP_EDGE",EDGE,{"disambiguationData":[OSD([sQuery(id+"F2.wireOp",EDGE,"E13.5.2")])],"isStart":true});
            var Q67;
            {var subQ0=sQuery(id+"F2.wireOp",EDGE,"E0");Q67=makeQuery(id+"F3.opExtrude","CAP_EDGE",EDGE,{"disambiguationData":[OSD([subQ0]),TDD([makeQuery(id+"F2.imprint","IMPRINT",EDGE,{"disambiguationData":[TD([[makeQuery(id+"F2.imprint","INTERSECT",VERTEX,{"derivedFrom":[subQ0,sQuery(id+"F2.wireOp",EDGE,"E13.4.2")]}),-1.0]])],"derivedFrom":subQ0})])],"isStart":true});}
            var Q68;
            Q68=makeQuery(id+"F3.opExtrude","CAP_EDGE",EDGE,{"disambiguationData":[OSD([sQuery(id+"F2.wireOp",EDGE,"E13.4.2")])],"isStart":true});
            var Q69;
            Q69=makeQuery(id+"F3.opExtrude","CAP_EDGE",EDGE,{"disambiguationData":[OSD([sQuery(id+"F2.wireOp",EDGE,"E13.4.0")])],"isStart":true});
            var Q70;
            {var subQ0=sQuery(id+"F2.wireOp",EDGE,"E0");Q70=makeQuery(id+"F3.opExtrude","CAP_EDGE",EDGE,{"disambiguationData":[OSD([subQ0]),TDD([makeQuery(id+"F2.imprint","IMPRINT",EDGE,{"disambiguationData":[TD([[makeQuery(id+"F2.imprint","INTERSECT",VERTEX,{"derivedFrom":[subQ0,sQuery(id+"F2.wireOp",EDGE,"E13.3.2")]}),-1.0]])],"derivedFrom":subQ0})])],"isStart":true});}
            var Q71;
            Q71=makeQuery(id+"F3.opExtrude","CAP_EDGE",EDGE,{"disambiguationData":[OSD([sQuery(id+"F2.wireOp",EDGE,"E13.3.2")])],"isStart":true});
            var Q72;
            Q72=makeQuery(id+"F3.opExtrude","CAP_EDGE",EDGE,{"disambiguationData":[OSD([sQuery(id+"F2.wireOp",EDGE,"E13.3.0")])],"isStart":true});
            var Q73;
            {var subQ0=sQuery(id+"F2.wireOp",EDGE,"E0");Q73=makeQuery(id+"F3.opExtrude","CAP_EDGE",EDGE,{"disambiguationData":[OSD([subQ0]),TDD([makeQuery(id+"F2.imprint","IMPRINT",EDGE,{"disambiguationData":[TD([[makeQuery(id+"F2.imprint","INTERSECT",VERTEX,{"derivedFrom":[subQ0,sQuery(id+"F2.wireOp",EDGE,"E13.2.2")]}),-1.0]])],"derivedFrom":subQ0})])],"isStart":true});}
            var Q74;
            Q74=makeQuery(id+"F3.opExtrude","CAP_EDGE",EDGE,{"disambiguationData":[OSD([sQuery(id+"F2.wireOp",EDGE,"E13.2.2")])],"isStart":true});
            var Q75;
            Q75=makeQuery(id+"F3.opExtrude","CAP_EDGE",EDGE,{"disambiguationData":[OSD([sQuery(id+"F2.wireOp",EDGE,"E13.2.0")])],"isStart":true});
            var Q76;
            Q76=makeQuery(id+"F3.opExtrude","CAP_EDGE",EDGE,{"disambiguationData":[OSD([sQuery(id+"F2.wireOp",EDGE,"E13.1.2")])],"isStart":true});
            var Q77;
            {var subQ0=sQuery(id+"F2.wireOp",EDGE,"E0");Q77=makeQuery(id+"F3.opExtrude","CAP_EDGE",EDGE,{"disambiguationData":[OSD([subQ0]),TDD([makeQuery(id+"F2.imprint","IMPRINT",EDGE,{"disambiguationData":[TD([[makeQuery(id+"F2.imprint","INTERSECT",VERTEX,{"derivedFrom":[subQ0,sQuery(id+"F2.wireOp",EDGE,"E13.1.2")]}),-1.0]])],"derivedFrom":subQ0})])],"isStart":true});}
            var Q78;
            Q78=makeQuery(id+"F3.opExtrude","CAP_EDGE",EDGE,{"disambiguationData":[OSD([sQuery(id+"F2.wireOp",EDGE,"E13.1.0")])],"isStart":true});
            var Q79;
            {var subQ0=sQuery(id+"F2.wireOp",EDGE,"E0");Q79=makeQuery(id+"F3.opExtrude","CAP_EDGE",EDGE,{"disambiguationData":[OSD([subQ0]),TDD([makeQuery(id+"F2.imprint","IMPRINT",EDGE,{"disambiguationData":[TD([[makeQuery(id+"F2.imprint","INTERSECT",VERTEX,{"derivedFrom":[subQ0,sQuery(id+"F2.wireOp",EDGE,"E11.MirrorCS")]}),-1.0]])],"derivedFrom":subQ0})])],"isStart":true});}
            var Q80;
            Q80=makeQuery(id+"F3.opExtrude","CAP_EDGE",EDGE,{"disambiguationData":[OSD([sQuery(id+"F2.wireOp",EDGE,"E11.MirrorCS")])],"isStart":true});
            var Q81;
            Q81=makeQuery(id+"F3.opExtrude","CAP_EDGE",EDGE,{"disambiguationData":[OSD([sQuery(id+"F2.wireOp",EDGE,"E10.trimOffspring")])],"isStart":true});
            var Q82;
            {var subQ0=sQuery(id+"F2.wireOp",EDGE,"E0");Q82=makeQuery(id+"F3.opExtrude","CAP_EDGE",EDGE,{"disambiguationData":[OSD([subQ0]),TDD([makeQuery(id+"F2.imprint","IMPRINT",EDGE,{"disambiguationData":[TD([[makeQuery(id+"F2.imprint","INTERSECT",VERTEX,{"derivedFrom":[subQ0,sQuery(id+"F2.wireOp",EDGE,"E10.trimOffspring")]}),1.0]])],"derivedFrom":subQ0})])],"isStart":true});}
            var Q83;
            Q83=makeQuery(id+"F3.opExtrude","CAP_EDGE",EDGE,{"disambiguationData":[OSD([sQuery(id+"F2.wireOp",EDGE,"E13.19.2")])],"isStart":true});
            var Q84;
            Q84=makeQuery(id+"F3.opExtrude","CAP_EDGE",EDGE,{"disambiguationData":[OSD([sQuery(id+"F2.wireOp",EDGE,"E13.19.0")])],"isStart":true});
            var Q85;
            {var subQ0=sQuery(id+"F2.wireOp",EDGE,"E0");Q85=makeQuery(id+"F3.opExtrude","CAP_EDGE",EDGE,{"disambiguationData":[OSD([subQ0]),TDD([makeQuery(id+"F2.imprint","IMPRINT",EDGE,{"disambiguationData":[TD([[makeQuery(id+"F2.imprint","INTERSECT",VERTEX,{"derivedFrom":[subQ0,sQuery(id+"F2.wireOp",EDGE,"E13.18.2")]}),-1.0]])],"derivedFrom":subQ0})])],"isStart":true});}
            var Q86;
            Q86=makeQuery(id+"F3.opExtrude","CAP_EDGE",EDGE,{"disambiguationData":[OSD([sQuery(id+"F2.wireOp",EDGE,"E13.18.2")])],"isStart":true});
            var Q87;
            Q87=makeQuery(id+"F3.opExtrude","CAP_EDGE",EDGE,{"disambiguationData":[OSD([sQuery(id+"F2.wireOp",EDGE,"E13.18.0")])],"isStart":true});
            var Q88;
            {var subQ0=sQuery(id+"F2.wireOp",EDGE,"E0");Q88=makeQuery(id+"F3.opExtrude","CAP_EDGE",EDGE,{"disambiguationData":[OSD([subQ0]),TDD([makeQuery(id+"F2.imprint","IMPRINT",EDGE,{"disambiguationData":[TD([[makeQuery(id+"F2.imprint","INTERSECT",VERTEX,{"derivedFrom":[subQ0,sQuery(id+"F2.wireOp",EDGE,"E13.17.2")]}),-1.0]])],"derivedFrom":subQ0})])],"isStart":true});}
            var Q89;
            Q89=makeQuery(id+"F3.opExtrude","CAP_EDGE",EDGE,{"disambiguationData":[OSD([sQuery(id+"F2.wireOp",EDGE,"E13.17.2")])],"isStart":true});
            var Q90;
            Q90=makeQuery(id+"F3.opExtrude","CAP_EDGE",EDGE,{"disambiguationData":[OSD([sQuery(id+"F2.wireOp",EDGE,"E13.17.0")])],"isStart":true});
            var Q91;
            {var subQ0=sQuery(id+"F2.wireOp",EDGE,"E0");Q91=makeQuery(id+"F3.opExtrude","CAP_EDGE",EDGE,{"disambiguationData":[OSD([subQ0]),TDD([makeQuery(id+"F2.imprint","IMPRINT",EDGE,{"disambiguationData":[TD([[makeQuery(id+"F2.imprint","INTERSECT",VERTEX,{"derivedFrom":[subQ0,sQuery(id+"F2.wireOp",EDGE,"E13.16.2")]}),-1.0]])],"derivedFrom":subQ0})])],"isStart":true});}
            var Q92;
            Q92=makeQuery(id+"F3.opExtrude","CAP_EDGE",EDGE,{"disambiguationData":[OSD([sQuery(id+"F2.wireOp",EDGE,"E13.16.2")])],"isStart":true});
            var Q93;
            Q93=makeQuery(id+"F3.opExtrude","CAP_EDGE",EDGE,{"disambiguationData":[OSD([sQuery(id+"F2.wireOp",EDGE,"E13.16.0")])],"isStart":true});
            var Q94;
            {var subQ0=sQuery(id+"F2.wireOp",EDGE,"E0");Q94=makeQuery(id+"F3.opExtrude","CAP_EDGE",EDGE,{"disambiguationData":[OSD([subQ0]),TDD([makeQuery(id+"F2.imprint","IMPRINT",EDGE,{"disambiguationData":[TD([[makeQuery(id+"F2.imprint","INTERSECT",VERTEX,{"derivedFrom":[subQ0,sQuery(id+"F2.wireOp",EDGE,"E13.15.2")]}),-1.0]])],"derivedFrom":subQ0})])],"isStart":true});}
            var Q95;
            Q95=makeQuery(id+"F3.opExtrude","CAP_EDGE",EDGE,{"disambiguationData":[OSD([sQuery(id+"F2.wireOp",EDGE,"E13.15.2")])],"isStart":true});
            var Q96;
            Q96=makeQuery(id+"F3.opExtrude","CAP_EDGE",EDGE,{"disambiguationData":[OSD([sQuery(id+"F2.wireOp",EDGE,"E13.15.0")])],"isStart":true});
            var Q97;
            {var subQ0=sQuery(id+"F2.wireOp",EDGE,"E0");Q97=makeQuery(id+"F3.opExtrude","CAP_EDGE",EDGE,{"disambiguationData":[OSD([subQ0]),TDD([makeQuery(id+"F2.imprint","IMPRINT",EDGE,{"disambiguationData":[TD([[makeQuery(id+"F2.imprint","INTERSECT",VERTEX,{"derivedFrom":[subQ0,sQuery(id+"F2.wireOp",EDGE,"E13.14.2")]}),-1.0]])],"derivedFrom":subQ0})])],"isStart":true});}
            var Q98;
            Q98=makeQuery(id+"F3.opExtrude","CAP_EDGE",EDGE,{"disambiguationData":[OSD([sQuery(id+"F2.wireOp",EDGE,"E13.14.2")])],"isStart":true});
            var Q99;
            Q99=makeQuery(id+"F3.opExtrude","CAP_EDGE",EDGE,{"disambiguationData":[OSD([sQuery(id+"F2.wireOp",EDGE,"E13.14.0")])],"isStart":true});
            var Q100;
            {var subQ0=sQuery(id+"F2.wireOp",EDGE,"E0");Q100=makeQuery(id+"F3.opExtrude","CAP_EDGE",EDGE,{"disambiguationData":[OSD([subQ0]),TDD([makeQuery(id+"F2.imprint","IMPRINT",EDGE,{"disambiguationData":[TD([[makeQuery(id+"F2.imprint","INTERSECT",VERTEX,{"derivedFrom":[subQ0,sQuery(id+"F2.wireOp",EDGE,"E13.13.2")]}),-1.0]])],"derivedFrom":subQ0})])],"isStart":true});}
            var Q101;
            Q101=makeQuery(id+"F3.opExtrude","CAP_EDGE",EDGE,{"disambiguationData":[OSD([sQuery(id+"F2.wireOp",EDGE,"E13.13.2")])],"isStart":true});
            var Q102;
            Q102=makeQuery(id+"F3.opExtrude","CAP_EDGE",EDGE,{"disambiguationData":[OSD([sQuery(id+"F2.wireOp",EDGE,"E13.13.0")])],"isStart":true});
            var Q103;
            {var subQ0=sQuery(id+"F2.wireOp",EDGE,"E0");Q103=makeQuery(id+"F3.opExtrude","CAP_EDGE",EDGE,{"disambiguationData":[OSD([subQ0]),TDD([makeQuery(id+"F2.imprint","IMPRINT",EDGE,{"disambiguationData":[TD([[makeQuery(id+"F2.imprint","INTERSECT",VERTEX,{"derivedFrom":[subQ0,sQuery(id+"F2.wireOp",EDGE,"E13.12.2")]}),-1.0]])],"derivedFrom":subQ0})])],"isStart":true});}
            var Q104;
            Q104=makeQuery(id+"F3.opExtrude","CAP_EDGE",EDGE,{"disambiguationData":[OSD([sQuery(id+"F2.wireOp",EDGE,"E13.12.2")])],"isStart":true});
            var Q105;
            Q105=makeQuery(id+"F3.opExtrude","CAP_EDGE",EDGE,{"disambiguationData":[OSD([sQuery(id+"F2.wireOp",EDGE,"E13.12.0")])],"isStart":true});
            var Q106;
            {var subQ0=sQuery(id+"F2.wireOp",EDGE,"E0");Q106=makeQuery(id+"F3.opExtrude","CAP_EDGE",EDGE,{"disambiguationData":[OSD([subQ0]),TDD([makeQuery(id+"F2.imprint","IMPRINT",EDGE,{"disambiguationData":[TD([[makeQuery(id+"F2.imprint","INTERSECT",VERTEX,{"derivedFrom":[subQ0,sQuery(id+"F2.wireOp",EDGE,"E13.11.2")]}),-1.0]])],"derivedFrom":subQ0})])],"isStart":true});}
            var Q107;
            Q107=makeQuery(id+"F3.opExtrude","CAP_EDGE",EDGE,{"disambiguationData":[OSD([sQuery(id+"F2.wireOp",EDGE,"E13.11.2")])],"isStart":true});
            var Q108;
            Q108=makeQuery(id+"F3.opExtrude","CAP_EDGE",EDGE,{"disambiguationData":[OSD([sQuery(id+"F2.wireOp",EDGE,"E13.11.0")])],"isStart":true});
            var Q109;
            {var subQ0=sQuery(id+"F2.wireOp",EDGE,"E0");Q109=makeQuery(id+"F3.opExtrude","CAP_EDGE",EDGE,{"disambiguationData":[OSD([subQ0]),TDD([makeQuery(id+"F2.imprint","IMPRINT",EDGE,{"disambiguationData":[TD([[makeQuery(id+"F2.imprint","INTERSECT",VERTEX,{"derivedFrom":[subQ0,sQuery(id+"F2.wireOp",EDGE,"E13.10.2")]}),-1.0]])],"derivedFrom":subQ0})])],"isStart":true});}
            var Q110;
            Q110=makeQuery(id+"F3.opExtrude","CAP_EDGE",EDGE,{"disambiguationData":[OSD([sQuery(id+"F2.wireOp",EDGE,"E13.10.2")])],"isStart":true});
            var Q111;
            Q111=makeQuery(id+"F3.opExtrude","CAP_EDGE",EDGE,{"disambiguationData":[OSD([sQuery(id+"F2.wireOp",EDGE,"E13.10.0")])],"isStart":true});
            var Q112;
            {var subQ0=sQuery(id+"F2.wireOp",EDGE,"E0");Q112=makeQuery(id+"F3.opExtrude","CAP_EDGE",EDGE,{"disambiguationData":[OSD([subQ0]),TDD([makeQuery(id+"F2.imprint","IMPRINT",EDGE,{"disambiguationData":[TD([[makeQuery(id+"F2.imprint","INTERSECT",VERTEX,{"derivedFrom":[subQ0,sQuery(id+"F2.wireOp",EDGE,"E13.9.2")]}),-1.0]])],"derivedFrom":subQ0})])],"isStart":true});}
            var Q113;
            Q113=makeQuery(id+"F3.opExtrude","CAP_EDGE",EDGE,{"disambiguationData":[OSD([sQuery(id+"F2.wireOp",EDGE,"E13.9.2")])],"isStart":true});
            var Q114;
            Q114=makeQuery(id+"F3.opExtrude","CAP_EDGE",EDGE,{"disambiguationData":[OSD([sQuery(id+"F2.wireOp",EDGE,"E13.9.0")])],"isStart":true});
            var Q115;
            {var subQ0=sQuery(id+"F2.wireOp",EDGE,"E0");Q115=makeQuery(id+"F3.opExtrude","CAP_EDGE",EDGE,{"disambiguationData":[OSD([subQ0]),TDD([makeQuery(id+"F2.imprint","IMPRINT",EDGE,{"disambiguationData":[TD([[makeQuery(id+"F2.imprint","INTERSECT",VERTEX,{"derivedFrom":[subQ0,sQuery(id+"F2.wireOp",EDGE,"E13.8.2")]}),-1.0]])],"derivedFrom":subQ0})])],"isStart":true});}
            var Q116;
            Q116=makeQuery(id+"F3.opExtrude","CAP_EDGE",EDGE,{"disambiguationData":[OSD([sQuery(id+"F2.wireOp",EDGE,"E13.8.2")])],"isStart":true});
            fillet(context, id + "F4", {"entities" : qUnion([Q0, Q1, Q2, Q3, Q4, Q5, Q6, Q7, Q8, Q9, Q10, Q11, Q12, Q13, Q14, Q15, Q16, Q17, Q18, Q19, Q20, Q21, Q22, Q23, Q24, Q25, Q26, Q27, Q28, Q29, Q30, Q31, Q32, Q33, Q34, Q35, Q36, Q37, Q38, Q39, Q40, Q41, Q42, Q43, Q44, Q45, Q46, Q47, Q48, Q49, Q50, Q51, Q52, Q53, Q54, Q55, Q56, Q57, Q58, Q59, Q60, Q61, Q62, Q63, Q64, Q65, Q66, Q67, Q68, Q69, Q70, Q71, Q72, Q73, Q74, Q75, Q76, Q77, Q78, Q79, Q80, Q81, Q82, Q83, Q84, Q85, Q86, Q87, Q88, Q89, Q90, Q91, Q92, Q93, Q94, Q95, Q96, Q97, Q98, Q99, Q100, Q101, Q102, Q103, Q104, Q105, Q106, Q107, Q108, Q109, Q110, Q111, Q112, Q113, Q114, Q115, Q116]), "radius" : (getVariable(context, 'TeethFillet')) * mm, "tangentPropagation" : true, "allowEdgeOverflow" : false});
        }
        {
            var Q0;
            Q0=makeQuery(id+"F3.opExtrude","SWEPT_BODY",BODY,{"disambiguationData":[OSD([sQuery(id+"F2.wireOp",EDGE,"E0"),sQuery(id+"F2.wireOp",EDGE,"E10.trimOffspring"),sQuery(id+"F2.wireOp",EDGE,"E11.MirrorCS"),sQuery(id+"F2.wireOp",EDGE,"E12"),sQuery(id+"F2.wireOp",EDGE,"E13.1.0"),sQuery(id+"F2.wireOp",EDGE,"E13.1.1"),sQuery(id+"F2.wireOp",EDGE,"E13.1.2"),sQuery(id+"F2.wireOp",EDGE,"E13.2.0"),sQuery(id+"F2.wireOp",EDGE,"E13.2.1"),sQuery(id+"F2.wireOp",EDGE,"E13.2.2"),sQuery(id+"F2.wireOp",EDGE,"E13.3.0"),sQuery(id+"F2.wireOp",EDGE,"E13.3.1"),sQuery(id+"F2.wireOp",EDGE,"E13.3.2"),sQuery(id+"F2.wireOp",EDGE,"E13.4.0"),sQuery(id+"F2.wireOp",EDGE,"E13.4.1"),sQuery(id+"F2.wireOp",EDGE,"E13.4.2"),sQuery(id+"F2.wireOp",EDGE,"E13.5.0"),sQuery(id+"F2.wireOp",EDGE,"E13.5.1"),sQuery(id+"F2.wireOp",EDGE,"E13.5.2"),sQuery(id+"F2.wireOp",EDGE,"E13.6.0"),sQuery(id+"F2.wireOp",EDGE,"E13.6.1"),sQuery(id+"F2.wireOp",EDGE,"E13.6.2"),sQuery(id+"F2.wireOp",EDGE,"E13.7.0"),sQuery(id+"F2.wireOp",EDGE,"E13.7.1"),sQuery(id+"F2.wireOp",EDGE,"E13.7.2"),sQuery(id+"F2.wireOp",EDGE,"E13.8.0"),sQuery(id+"F2.wireOp",EDGE,"E13.8.1"),sQuery(id+"F2.wireOp",EDGE,"E13.8.2"),sQuery(id+"F2.wireOp",EDGE,"E13.9.0"),sQuery(id+"F2.wireOp",EDGE,"E13.9.1"),sQuery(id+"F2.wireOp",EDGE,"E13.9.2"),sQuery(id+"F2.wireOp",EDGE,"E13.10.0"),sQuery(id+"F2.wireOp",EDGE,"E13.10.1"),sQuery(id+"F2.wireOp",EDGE,"E13.10.2"),sQuery(id+"F2.wireOp",EDGE,"E13.11.0"),sQuery(id+"F2.wireOp",EDGE,"E13.11.1"),sQuery(id+"F2.wireOp",EDGE,"E13.11.2"),sQuery(id+"F2.wireOp",EDGE,"E13.12.0"),sQuery(id+"F2.wireOp",EDGE,"E13.12.1"),sQuery(id+"F2.wireOp",EDGE,"E13.12.2"),sQuery(id+"F2.wireOp",EDGE,"E13.13.0"),sQuery(id+"F2.wireOp",EDGE,"E13.13.1"),sQuery(id+"F2.wireOp",EDGE,"E13.13.2"),sQuery(id+"F2.wireOp",EDGE,"E13.14.0"),sQuery(id+"F2.wireOp",EDGE,"E13.14.1"),sQuery(id+"F2.wireOp",EDGE,"E13.14.2"),sQuery(id+"F2.wireOp",EDGE,"E13.15.0"),sQuery(id+"F2.wireOp",EDGE,"E13.15.1"),sQuery(id+"F2.wireOp",EDGE,"E13.15.2"),sQuery(id+"F2.wireOp",EDGE,"E13.16.0"),sQuery(id+"F2.wireOp",EDGE,"E13.16.1"),sQuery(id+"F2.wireOp",EDGE,"E13.16.2"),sQuery(id+"F2.wireOp",EDGE,"E13.17.0"),sQuery(id+"F2.wireOp",EDGE,"E13.17.1"),sQuery(id+"F2.wireOp",EDGE,"E13.17.2"),sQuery(id+"F2.wireOp",EDGE,"E13.18.0"),sQuery(id+"F2.wireOp",EDGE,"E13.18.1"),sQuery(id+"F2.wireOp",EDGE,"E13.18.2"),sQuery(id+"F2.wireOp",EDGE,"E13.19.0"),sQuery(id+"F2.wireOp",EDGE,"E13.19.1"),sQuery(id+"F2.wireOp",EDGE,"E13.19.2"),sQuery(id+"F2.wireOp",EDGE,"E14")])]});
            transform(context, id + "F5", {"entities" : qUnion([Q0]), "transformType" : TransformType.TRANSLATION_3D, "dx" : 0 * mm, "dy" : 0 * mm, "dz" : 0 * mm, "makeCopy" : true});
        }
    });
